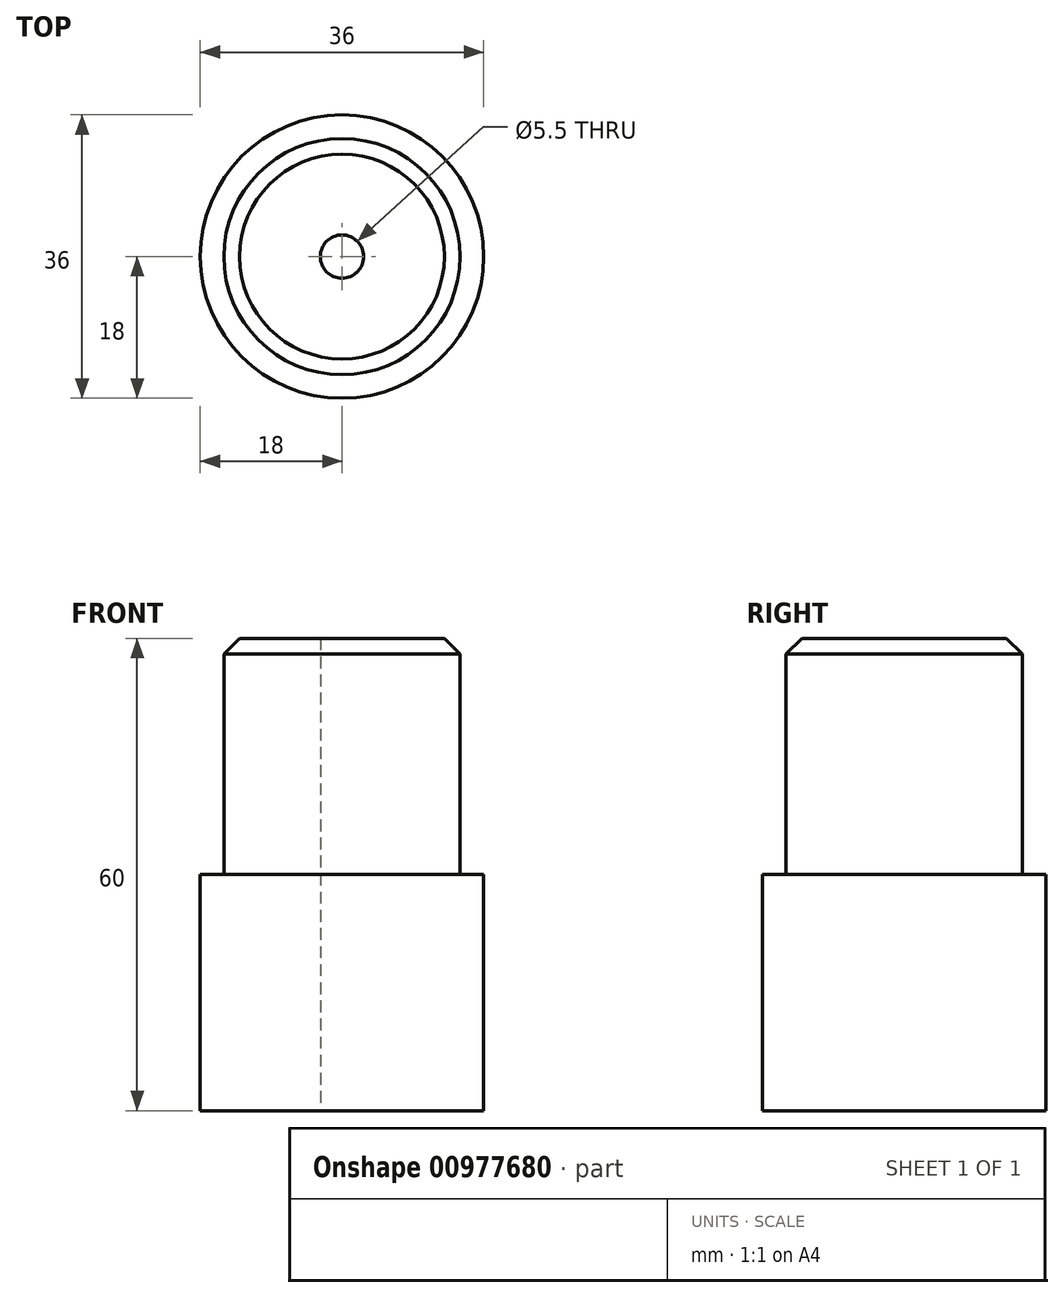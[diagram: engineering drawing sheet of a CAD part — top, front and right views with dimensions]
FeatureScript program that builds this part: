
annotation { "Feature Type Name" : "Feature", "Feature Type Description" : "" }
export const myFeature = defineFeature(function(context is Context, id is Id, definition is map)
    precondition{}
    {
        {
            var Q0;
            Q0=qCreatedBy(makeId("Top.planeOp"),FACE);
            var sketch = newSketch(context, id + "F0", { "sketchPlane" : qUnion([Q0])});
            skCircle(sketch, "E0", {"center": v(0, 0) * mm, "radius": 18 * mm});
            skSolve(sketch);
        }
        {
            var Q0;
            Q0 = qSketchRegion(id + "F0", true);
            extrude(context, id + "F1", {"entities" : qUnion([Q0]), "depth" : 30 * mm, "offsetDistance" : 25 * mm});
        }
        {
            var Q0;
            Q0=makeQuery(id+"F1.opExtrude","CAP_FACE",FACE,{"disambiguationData":[OSD([sQuery(id+"F0.wireOp",EDGE,"E0")])],"isStart":false});
            var sketch = newSketch(context, id + "F2", { "sketchPlane" : qUnion([Q0])});
            skCircle(sketch, "E1", {"center": v(0, 0) * mm, "radius": 15 * mm});
            skSolve(sketch);
        }
        {
            var Q0;
            Q0 = qSketchRegion(id + "F2", true);
            extrude(context, id + "F3", {"entities" : qUnion([Q0]), "operationType" : NewBodyOperationType.ADD, "depth" : 30 * mm, "offsetDistance" : 25 * mm});
        }
        {
            var Q0;
            Q0=makeQuery(id+"F1.opExtrude","CAP_FACE",FACE,{"disambiguationData":[OSD([sQuery(id+"F0.wireOp",EDGE,"E0")])],"isStart":true});
            var sketch = newSketch(context, id + "F4", { "sketchPlane" : qUnion([Q0])});
            skPoint(sketch, "E2", {"position": v(0, 0) * mm});
            skSolve(sketch);
        }
        {
            var Q0;
            Q0=sQuery(id+"F4.wireOp",VERTEX,"E2");
            var Q1;
            Q1=makeQuery(id+"F1.opExtrude","SWEPT_BODY",BODY,{"disambiguationData":[OSD([sQuery(id+"F0.wireOp",EDGE,"E0")])]});
            hole(context, id + "F5", {"style" : HoleStyle.SIMPLE, "endStyle" : HoleEndStyle.THROUGH, "standardTappedOrClearance" : lookupTablePath({ "fit" : "Normal", "standard" : "ISO", "size" : "M5", "type" : "Clearance" }), "standardBlindInLast" : lookupTablePath({ "fit" : "Normal", "standard" : "ISO", "engagement" : "75%", "pitch" : "0.8 mm", "size" : "M5", "type" : "Clearance & tapped" }), "holeDiameter" : 5.5 * mm, "majorDiameter" : 5 * mm, "isTappedThrough" : true, "tappedDepth" : 12 * mm, "tapClearance" : 3, "locations" : qUnion([Q0]), "scope" : qUnion([Q1])});
        }
        {
            var Q0;
            Q0=makeQuery(id+"F3.opExtrude","CAP_EDGE",EDGE,{"disambiguationData":[OSD([sQuery(id+"F2.wireOp",EDGE,"E1")])],"isStart":false});
            chamfer(context, id + "F6", {"entities" : qUnion([Q0]), "width" : 2 * mm, "tangentPropagation" : true});
        }
    });
